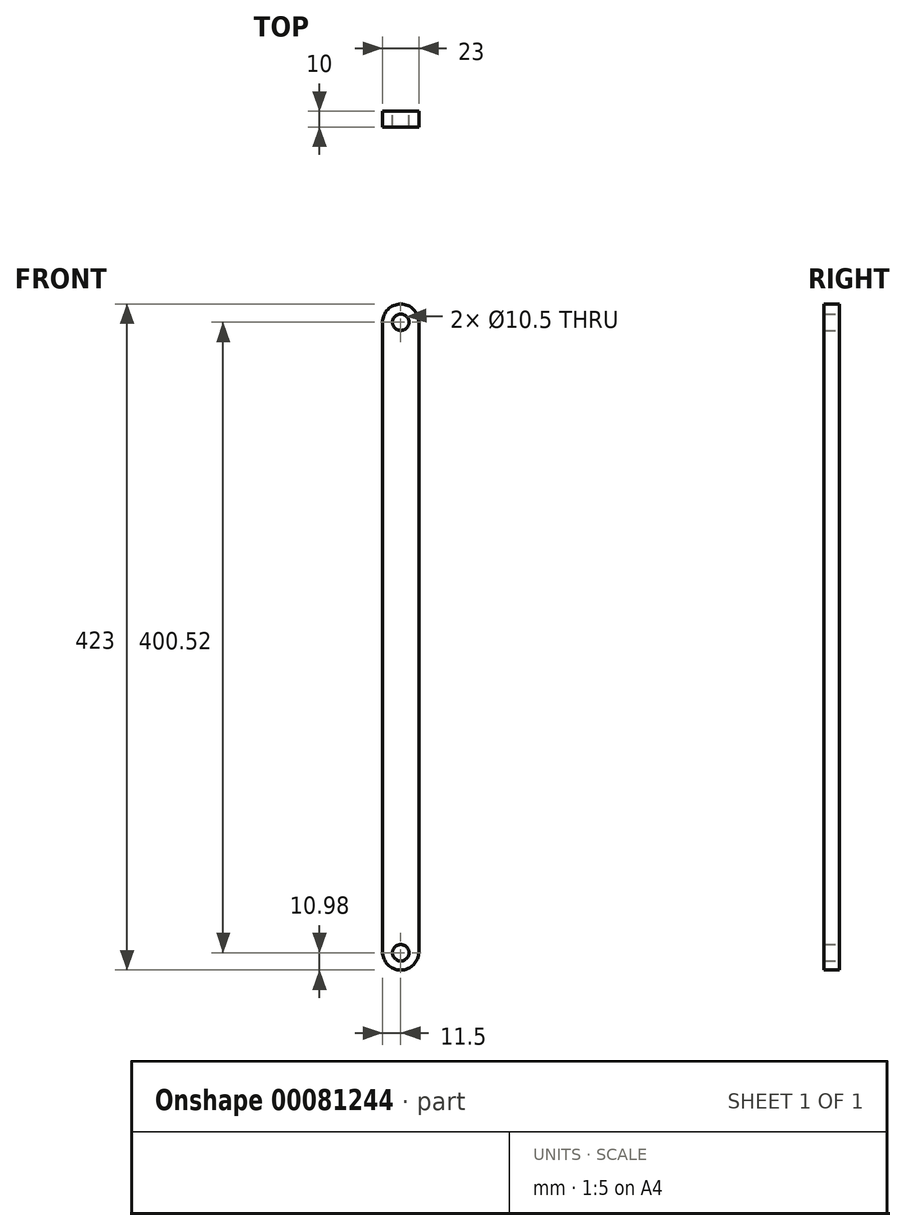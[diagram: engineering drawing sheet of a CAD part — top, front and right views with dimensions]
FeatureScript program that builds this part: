
annotation { "Feature Type Name" : "Feature", "Feature Type Description" : "" }
export const myFeature = defineFeature(function(context is Context, id is Id, definition is map)
    precondition{}
    {
        {
            var Q0;
            Q0=qCreatedBy(makeId("Front.planeOp"),FACE);
            var sketch = newSketch(context, id + "F0", { "sketchPlane" : qUnion([Q0])});
            skLineSegment(sketch, "E0", {"start": v(0, 56.16) * mm, "end": v(0, -56.16) * mm, "construction": true});
            skLineSegment(sketch, "E1", {"start": v(11.5, 0) * mm, "end": v(-11.5, 0) * mm, "construction": true});
            skLineSegment(sketch, "E2", {"start": v(-11.5, 344.36) * mm, "end": v(-11.5, -55.64) * mm});
            skLineSegment(sketch, "E3.MirrorCS", {"start": v(11.5, 344.36) * mm, "end": v(11.5, -55.64) * mm});
            skPoint(sketch, "E4.orphan", {"position": v(17.94, 0) * mm});
            skArc(sketch, "E5", {"start": v(-11.5, -55.64) * mm, "mid": v(0, -67.14) * mm, "end": v(11.5, -55.64) * mm});
            skArc(sketch, "E6", {"start": v(11.5, 344.36) * mm, "mid": v(0, 355.86) * mm, "end": v(-11.5, 344.36) * mm});
            skCircle(sketch, "E7", {"center": v(0, 344.36) * mm, "radius": 5.25 * mm});
            skCircle(sketch, "E8", {"center": v(0, -55.64) * mm, "radius": 0.52 * mm});
            skCircle(sketch, "E9", {"center": v(0, -56.16) * mm, "radius": 5.25 * mm});
            skSolve(sketch);
        }
        {
            var Q0;
            Q0=makeQuery(id+"F0.imprint","IMPRINT",FACE,{"disambiguationData":[TD([[makeQuery(id+"F0.imprint","IMPRINT",EDGE,{"derivedFrom":sQuery(id+"F0.wireOp",EDGE,"E2")}),1.0]])]});
            extrude(context, id + "F1", {"entities" : qUnion([Q0]), "depth" : 5 * mm, "hasSecondDirection" : true, "secondDirectionOppositeDirection" : true, "secondDirectionDepth" : 5 * mm});
        }
    });
